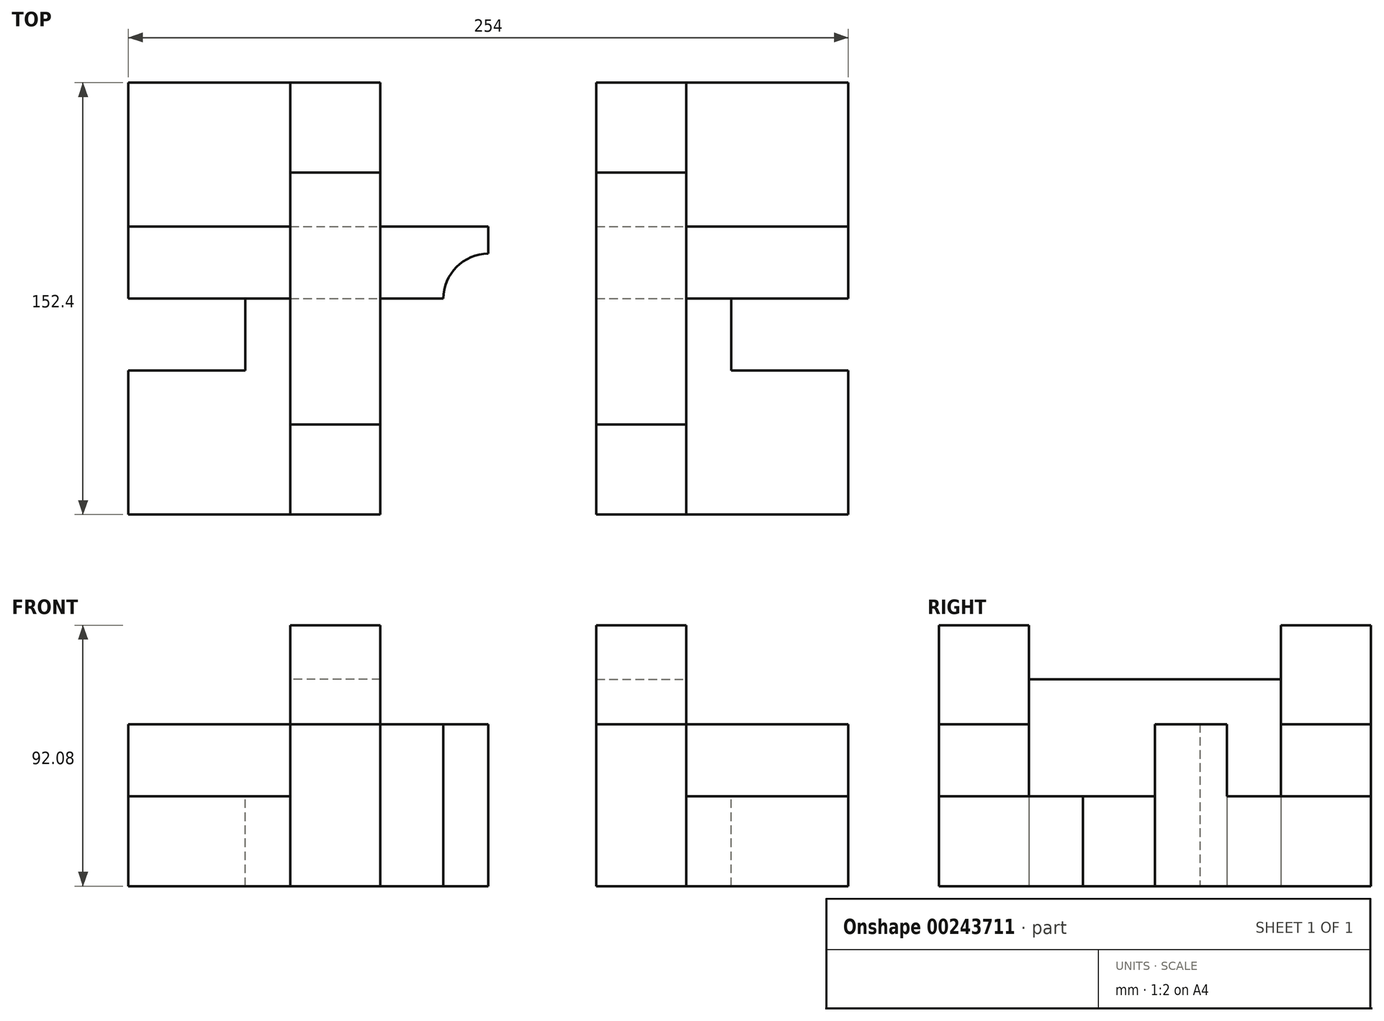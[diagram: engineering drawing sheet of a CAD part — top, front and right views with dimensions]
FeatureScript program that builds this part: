
annotation { "Feature Type Name" : "Feature", "Feature Type Description" : "" }
export const myFeature = defineFeature(function(context is Context, id is Id, definition is map)
    precondition{}
    {
        {
            var Q0;
            Q0=qCreatedBy(makeId("Top.planeOp"),FACE);
            var sketch = newSketch(context, id + "F0", { "sketchPlane" : qUnion([Q0])});
            skLineSegment(sketch, "E0.bottom", {"start": v(127, -76.2) * mm, "end": v(-127, -76.2) * mm});
            skLineSegment(sketch, "E0.top", {"start": v(127, 76.2) * mm, "end": v(-127, 76.2) * mm});
            skLineSegment(sketch, "E0.left", {"start": v(127, -76.2) * mm, "end": v(127, 76.2) * mm});
            skLineSegment(sketch, "E0.right", {"start": v(-127, -76.2) * mm, "end": v(-127, 76.2) * mm});
            skPoint(sketch, "E0.middle", {"position": v(0, 0) * mm});
            skLineSegment(sketch, "E1", {"start": v(-127, 25.4) * mm, "end": v(127, 25.4) * mm});
            skLineSegment(sketch, "E2", {"start": v(0, 0) * mm, "end": v(0, 76.2) * mm});
            skLineSegment(sketch, "E3", {"start": v(0, 76.2) * mm, "end": v(0, -76.2) * mm});
            skLineSegment(sketch, "E4", {"start": v(0, -76.2) * mm, "end": v(0, 0) * mm});
            skLineSegment(sketch, "E5", {"start": v(69.85, 76.2) * mm, "end": v(69.85, 0) * mm});
            skLineSegment(sketch, "E6", {"start": v(38.1, 76.2) * mm, "end": v(38.1, 0) * mm});
            skLineSegment(sketch, "E7", {"start": v(38.1, 44.45) * mm, "end": v(69.85, 44.45) * mm});
            skLineSegment(sketch, "E8.MirrorCS", {"start": v(-38.1, 76.2) * mm, "end": v(-38.1, 0) * mm});
            skLineSegment(sketch, "E9.MirrorCS", {"start": v(-38.1, 44.45) * mm, "end": v(-69.85, 44.45) * mm});
            skLineSegment(sketch, "E10.MirrorCS", {"start": v(-69.85, 76.2) * mm, "end": v(-69.85, 0) * mm});
            skLineSegment(sketch, "E11", {"start": v(-127, 0) * mm, "end": v(127, 0) * mm});
            skLineSegment(sketch, "E12.MirrorCS", {"start": v(-69.85, -76.2) * mm, "end": v(-69.85, 0) * mm});
            skLineSegment(sketch, "E13.MirrorCS", {"start": v(-38.1, -44.45) * mm, "end": v(-69.85, -44.45) * mm});
            skLineSegment(sketch, "E14.MirrorCS", {"start": v(-38.1, -76.2) * mm, "end": v(-38.1, 0) * mm});
            skLineSegment(sketch, "E15.MirrorCS", {"start": v(38.1, -76.2) * mm, "end": v(38.1, 0) * mm});
            skLineSegment(sketch, "E16.MirrorCS", {"start": v(38.1, -44.45) * mm, "end": v(69.85, -44.45) * mm});
            skLineSegment(sketch, "E17.MirrorCS", {"start": v(69.85, -76.2) * mm, "end": v(69.85, 0) * mm});
            skLineSegment(sketch, "E18.MirrorCS", {"start": v(-127, -25.4) * mm, "end": v(127, -25.4) * mm});
            skLineSegment(sketch, "E19", {"start": v(85.72, 25.4) * mm, "end": v(85.72, -25.4) * mm});
            skLineSegment(sketch, "E20.MirrorCS", {"start": v(-85.72, 25.4) * mm, "end": v(-85.72, -25.4) * mm});
            skCircle(sketch, "E21", {"center": v(0, 0) * mm, "radius": 15.88 * mm});
            skSolve(sketch);
        }
        {
            var Q0;
            {var subQ4=sQuery(id+"F0.wireOp",EDGE,"E0.right");var subQ6=sQuery(id+"F0.wireOp",EDGE,"E0.top");var subQ7=makeQuery(id+"F0.imprint","INTERSECT",VERTEX,{"derivedFrom":[subQ6,subQ4]});Q0=makeQuery(id+"F0.imprint","IMPRINT",FACE,{"disambiguationData":[TD([[makeQuery(id+"F0.imprint","IMPRINT",EDGE,{"disambiguationData":[TD([[subQ7,1.0]])],"derivedFrom":subQ6}),1.0]])]});}
            var Q1;
            {var subQ4=sQuery(id+"F0.wireOp",EDGE,"E0.bottom");var subQ6=sQuery(id+"F0.wireOp",EDGE,"E0.right");var subQ7=makeQuery(id+"F0.imprint","INTERSECT",VERTEX,{"derivedFrom":[subQ4,subQ6]});Q1=makeQuery(id+"F0.imprint","IMPRINT",FACE,{"disambiguationData":[TD([[makeQuery(id+"F0.imprint","IMPRINT",EDGE,{"disambiguationData":[TD([[subQ7,1.0]])],"derivedFrom":subQ4}),-1.0]])]});}
            var Q2;
            {var subQ4=sQuery(id+"F0.wireOp",EDGE,"E0.bottom");var subQ6=sQuery(id+"F0.wireOp",EDGE,"E0.left");var subQ7=makeQuery(id+"F0.imprint","INTERSECT",VERTEX,{"derivedFrom":[subQ4,subQ6]});Q2=makeQuery(id+"F0.imprint","IMPRINT",FACE,{"disambiguationData":[TD([[makeQuery(id+"F0.imprint","IMPRINT",EDGE,{"disambiguationData":[TD([[subQ7,-1.0]])],"derivedFrom":subQ4}),-1.0]])]});}
            var Q3;
            {var subQ4=sQuery(id+"F0.wireOp",EDGE,"E0.left");var subQ5=sQuery(id+"F0.wireOp",EDGE,"E0.top");var subQ6=makeQuery(id+"F0.imprint","INTERSECT",VERTEX,{"derivedFrom":[subQ5,subQ4]});Q3=makeQuery(id+"F0.imprint","IMPRINT",FACE,{"disambiguationData":[TD([[makeQuery(id+"F0.imprint","IMPRINT",EDGE,{"disambiguationData":[TD([[subQ6,-1.0]])],"derivedFrom":subQ5}),1.0]])]});}
            var Q4;
            {var subQ0=sQuery(id+"F0.wireOp",EDGE,"E19");var subQ1=sQuery(id+"F0.wireOp",EDGE,"E1");var subQ2=makeQuery(id+"F0.imprint","INTERSECT",VERTEX,{"derivedFrom":[subQ1,subQ0]});Q4=makeQuery(id+"F0.imprint","IMPRINT",FACE,{"disambiguationData":[TD([[makeQuery(id+"F0.imprint","IMPRINT",EDGE,{"disambiguationData":[TD([[subQ2,1.0]])],"derivedFrom":subQ1}),-1.0]])]});}
            var Q5;
            {var subQ3=sQuery(id+"F0.wireOp",EDGE,"E19");var subQ5=sQuery(id+"F0.wireOp",EDGE,"E18.MirrorCS");var subQ7=makeQuery(id+"F0.imprint","INTERSECT",VERTEX,{"derivedFrom":[subQ5,subQ3]});Q5=makeQuery(id+"F0.imprint","IMPRINT",FACE,{"disambiguationData":[TD([[makeQuery(id+"F0.imprint","IMPRINT",EDGE,{"disambiguationData":[TD([[subQ7,1.0]])],"derivedFrom":subQ5}),1.0]])]});}
            var Q6;
            {var subQ0=sQuery(id+"F0.wireOp",EDGE,"E20.MirrorCS");var subQ1=sQuery(id+"F0.wireOp",EDGE,"E1");var subQ2=makeQuery(id+"F0.imprint","INTERSECT",VERTEX,{"derivedFrom":[subQ1,subQ0]});Q6=makeQuery(id+"F0.imprint","IMPRINT",FACE,{"disambiguationData":[TD([[makeQuery(id+"F0.imprint","IMPRINT",EDGE,{"disambiguationData":[TD([[subQ2,-1.0]])],"derivedFrom":subQ1}),-1.0]])]});}
            var Q7;
            {var subQ3=sQuery(id+"F0.wireOp",EDGE,"E20.MirrorCS");var subQ5=sQuery(id+"F0.wireOp",EDGE,"E18.MirrorCS");var subQ6=makeQuery(id+"F0.imprint","INTERSECT",VERTEX,{"derivedFrom":[subQ5,subQ3]});Q7=makeQuery(id+"F0.imprint","IMPRINT",FACE,{"disambiguationData":[TD([[makeQuery(id+"F0.imprint","IMPRINT",EDGE,{"disambiguationData":[TD([[subQ6,-1.0]])],"derivedFrom":subQ5}),1.0]])]});}
            extrude(context, id + "F1", {"entities" : qUnion([Q0, Q1, Q2, Q3, Q4, Q5, Q6, Q7]), "depth" : 31.75 * mm});
        }
        {
            var Q0;
            {var subQ0=sQuery(id+"F0.wireOp",EDGE,"E3");var subQ1=sQuery(id+"F0.wireOp",EDGE,"E0.top");var subQ2=makeQuery(id+"F0.imprint","INTERSECT",VERTEX,{"derivedFrom":[subQ1,subQ0]});Q0=makeQuery(id+"F0.imprint","IMPRINT",FACE,{"disambiguationData":[TD([[makeQuery(id+"F0.imprint","IMPRINT",EDGE,{"disambiguationData":[TD([[subQ2,-1.0]])],"derivedFrom":subQ1}),1.0]])]});}
            var Q1;
            {var subQ1=sQuery(id+"F0.wireOp",EDGE,"E0.top");var subQ4=sQuery(id+"F0.wireOp",EDGE,"E3");var subQ8=makeQuery(id+"F0.imprint","INTERSECT",VERTEX,{"derivedFrom":[subQ1,subQ4]});Q1=makeQuery(id+"F0.imprint","IMPRINT",FACE,{"disambiguationData":[TD([[makeQuery(id+"F0.imprint","IMPRINT",EDGE,{"disambiguationData":[TD([[subQ8,1.0]])],"derivedFrom":subQ1}),1.0]])]});}
            var Q2;
            {var subQ1=sQuery(id+"F0.wireOp",EDGE,"E8.MirrorCS");var subQ5=sQuery(id+"F0.wireOp",EDGE,"E1");var subQ6=makeQuery(id+"F0.imprint","INTERSECT",VERTEX,{"derivedFrom":[subQ5,subQ1]});Q2=makeQuery(id+"F0.imprint","IMPRINT",FACE,{"disambiguationData":[TD([[makeQuery(id+"F0.imprint","IMPRINT",EDGE,{"disambiguationData":[TD([[subQ6,-1.0]])],"derivedFrom":subQ5}),-1.0]])]});}
            var Q3;
            {var subQ5=sQuery(id+"F0.wireOp",EDGE,"E3");var subQ6=sQuery(id+"F0.wireOp",EDGE,"E1");var subQ7=makeQuery(id+"F0.imprint","INTERSECT",VERTEX,{"derivedFrom":[subQ6,subQ5]});Q3=makeQuery(id+"F0.imprint","IMPRINT",FACE,{"disambiguationData":[TD([[makeQuery(id+"F0.imprint","IMPRINT",EDGE,{"disambiguationData":[TD([[subQ7,-1.0]])],"derivedFrom":subQ6}),-1.0]])]});}
            var Q4;
            {var subQ0=sQuery(id+"F0.wireOp",EDGE,"E18.MirrorCS");var subQ1=sQuery(id+"F0.wireOp",EDGE,"E4");var subQ2=makeQuery(id+"F0.imprint","INTERSECT",VERTEX,{"derivedFrom":[subQ1,subQ0]});Q4=makeQuery(id+"F0.imprint","IMPRINT",FACE,{"disambiguationData":[TD([[makeQuery(id+"F0.imprint","IMPRINT",EDGE,{"disambiguationData":[TD([[subQ2,-1.0]])],"derivedFrom":subQ1}),1.0]])]});}
            var Q5;
            {var subQ0=sQuery(id+"F0.wireOp",EDGE,"E18.MirrorCS");var subQ1=sQuery(id+"F0.wireOp",EDGE,"E4");var subQ2=makeQuery(id+"F0.imprint","INTERSECT",VERTEX,{"derivedFrom":[subQ1,subQ0]});Q5=makeQuery(id+"F0.imprint","IMPRINT",FACE,{"disambiguationData":[TD([[makeQuery(id+"F0.imprint","IMPRINT",EDGE,{"disambiguationData":[TD([[subQ2,-1.0]])],"derivedFrom":subQ1}),-1.0]])]});}
            var Q6;
            {var subQ4=sQuery(id+"F0.wireOp",EDGE,"E0.bottom");var subQ6=sQuery(id+"F0.wireOp",EDGE,"E4");var subQ7=makeQuery(id+"F0.imprint","INTERSECT",VERTEX,{"derivedFrom":[subQ4,subQ6]});Q6=makeQuery(id+"F0.imprint","IMPRINT",FACE,{"disambiguationData":[TD([[makeQuery(id+"F0.imprint","IMPRINT",EDGE,{"disambiguationData":[TD([[subQ7,-1.0]])],"derivedFrom":subQ4}),-1.0]])]});}
            var Q7;
            {var subQ4=sQuery(id+"F0.wireOp",EDGE,"E0.bottom");var subQ6=sQuery(id+"F0.wireOp",EDGE,"E4");var subQ7=makeQuery(id+"F0.imprint","INTERSECT",VERTEX,{"derivedFrom":[subQ4,subQ6]});Q7=makeQuery(id+"F0.imprint","IMPRINT",FACE,{"disambiguationData":[TD([[makeQuery(id+"F0.imprint","IMPRINT",EDGE,{"disambiguationData":[TD([[subQ7,1.0]])],"derivedFrom":subQ4}),-1.0]])]});}
            extrude(context, id + "F2", {"entities" : qUnion([Q0, Q1, Q2, Q3, Q4, Q5, Q6, Q7]), "operationType" : NewBodyOperationType.ADD, "depth" : 57.15 * mm});
        }
        {
            var Q0;
            {var subQ5=sQuery(id+"F0.wireOp",EDGE,"E9.MirrorCS");Q0=makeQuery(id+"F0.imprint","IMPRINT",FACE,{"disambiguationData":[TD([[makeQuery(id+"F0.imprint","IMPRINT",EDGE,{"derivedFrom":subQ5}),-1.0]])]});}
            var Q1;
            {var subQ5=sQuery(id+"F0.wireOp",EDGE,"E13.MirrorCS");Q1=makeQuery(id+"F0.imprint","IMPRINT",FACE,{"disambiguationData":[TD([[makeQuery(id+"F0.imprint","IMPRINT",EDGE,{"derivedFrom":subQ5}),1.0]])]});}
            var Q2;
            {var subQ5=sQuery(id+"F0.wireOp",EDGE,"E16.MirrorCS");Q2=makeQuery(id+"F0.imprint","IMPRINT",FACE,{"disambiguationData":[TD([[makeQuery(id+"F0.imprint","IMPRINT",EDGE,{"derivedFrom":subQ5}),-1.0]])]});}
            var Q3;
            {var subQ5=sQuery(id+"F0.wireOp",EDGE,"E7");Q3=makeQuery(id+"F0.imprint","IMPRINT",FACE,{"disambiguationData":[TD([[makeQuery(id+"F0.imprint","IMPRINT",EDGE,{"derivedFrom":subQ5}),1.0]])]});}
            extrude(context, id + "F3", {"entities" : qUnion([Q0, Q1, Q2, Q3]), "depth" : 92.07 * mm});
        }
        {
            var Q0;
            {var subQ5=sQuery(id+"F0.wireOp",EDGE,"E9.MirrorCS");Q0=makeQuery(id+"F0.imprint","IMPRINT",FACE,{"disambiguationData":[TD([[makeQuery(id+"F0.imprint","IMPRINT",EDGE,{"derivedFrom":subQ5}),1.0]])]});}
            var Q1;
            {var subQ0=sQuery(id+"F0.wireOp",EDGE,"E10.MirrorCS");var subQ1=sQuery(id+"F0.wireOp",EDGE,"E1");var subQ2=makeQuery(id+"F0.imprint","INTERSECT",VERTEX,{"derivedFrom":[subQ1,subQ0]});Q1=makeQuery(id+"F0.imprint","IMPRINT",FACE,{"disambiguationData":[TD([[makeQuery(id+"F0.imprint","IMPRINT",EDGE,{"disambiguationData":[TD([[subQ2,-1.0]])],"derivedFrom":subQ1}),-1.0]])]});}
            var Q2;
            {var subQ3=sQuery(id+"F0.wireOp",EDGE,"E12.MirrorCS");var subQ5=sQuery(id+"F0.wireOp",EDGE,"E18.MirrorCS");var subQ7=makeQuery(id+"F0.imprint","INTERSECT",VERTEX,{"derivedFrom":[subQ3,subQ5]});Q2=makeQuery(id+"F0.imprint","IMPRINT",FACE,{"disambiguationData":[TD([[makeQuery(id+"F0.imprint","IMPRINT",EDGE,{"disambiguationData":[TD([[subQ7,-1.0]])],"derivedFrom":subQ5}),1.0]])]});}
            var Q3;
            {var subQ0=sQuery(id+"F0.wireOp",EDGE,"E13.MirrorCS");Q3=makeQuery(id+"F0.imprint","IMPRINT",FACE,{"disambiguationData":[TD([[makeQuery(id+"F0.imprint","IMPRINT",EDGE,{"derivedFrom":subQ0}),-1.0]])]});}
            var Q4;
            {var subQ0=sQuery(id+"F0.wireOp",EDGE,"E16.MirrorCS");Q4=makeQuery(id+"F0.imprint","IMPRINT",FACE,{"disambiguationData":[TD([[makeQuery(id+"F0.imprint","IMPRINT",EDGE,{"derivedFrom":subQ0}),1.0]])]});}
            var Q5;
            {var subQ3=sQuery(id+"F0.wireOp",EDGE,"E15.MirrorCS");var subQ5=sQuery(id+"F0.wireOp",EDGE,"E18.MirrorCS");var subQ7=makeQuery(id+"F0.imprint","INTERSECT",VERTEX,{"derivedFrom":[subQ3,subQ5]});Q5=makeQuery(id+"F0.imprint","IMPRINT",FACE,{"disambiguationData":[TD([[makeQuery(id+"F0.imprint","IMPRINT",EDGE,{"disambiguationData":[TD([[subQ7,-1.0]])],"derivedFrom":subQ5}),1.0]])]});}
            var Q6;
            {var subQ0=sQuery(id+"F0.wireOp",EDGE,"E6");var subQ1=sQuery(id+"F0.wireOp",EDGE,"E1");var subQ2=makeQuery(id+"F0.imprint","INTERSECT",VERTEX,{"derivedFrom":[subQ1,subQ0]});Q6=makeQuery(id+"F0.imprint","IMPRINT",FACE,{"disambiguationData":[TD([[makeQuery(id+"F0.imprint","IMPRINT",EDGE,{"disambiguationData":[TD([[subQ2,-1.0]])],"derivedFrom":subQ1}),-1.0]])]});}
            var Q7;
            {var subQ5=sQuery(id+"F0.wireOp",EDGE,"E7");Q7=makeQuery(id+"F0.imprint","IMPRINT",FACE,{"disambiguationData":[TD([[makeQuery(id+"F0.imprint","IMPRINT",EDGE,{"derivedFrom":subQ5}),-1.0]])]});}
            extrude(context, id + "F4", {"entities" : qUnion([Q0, Q1, Q2, Q3, Q4, Q5, Q6, Q7]), "depth" : 73.02 * mm});
        }
    });
